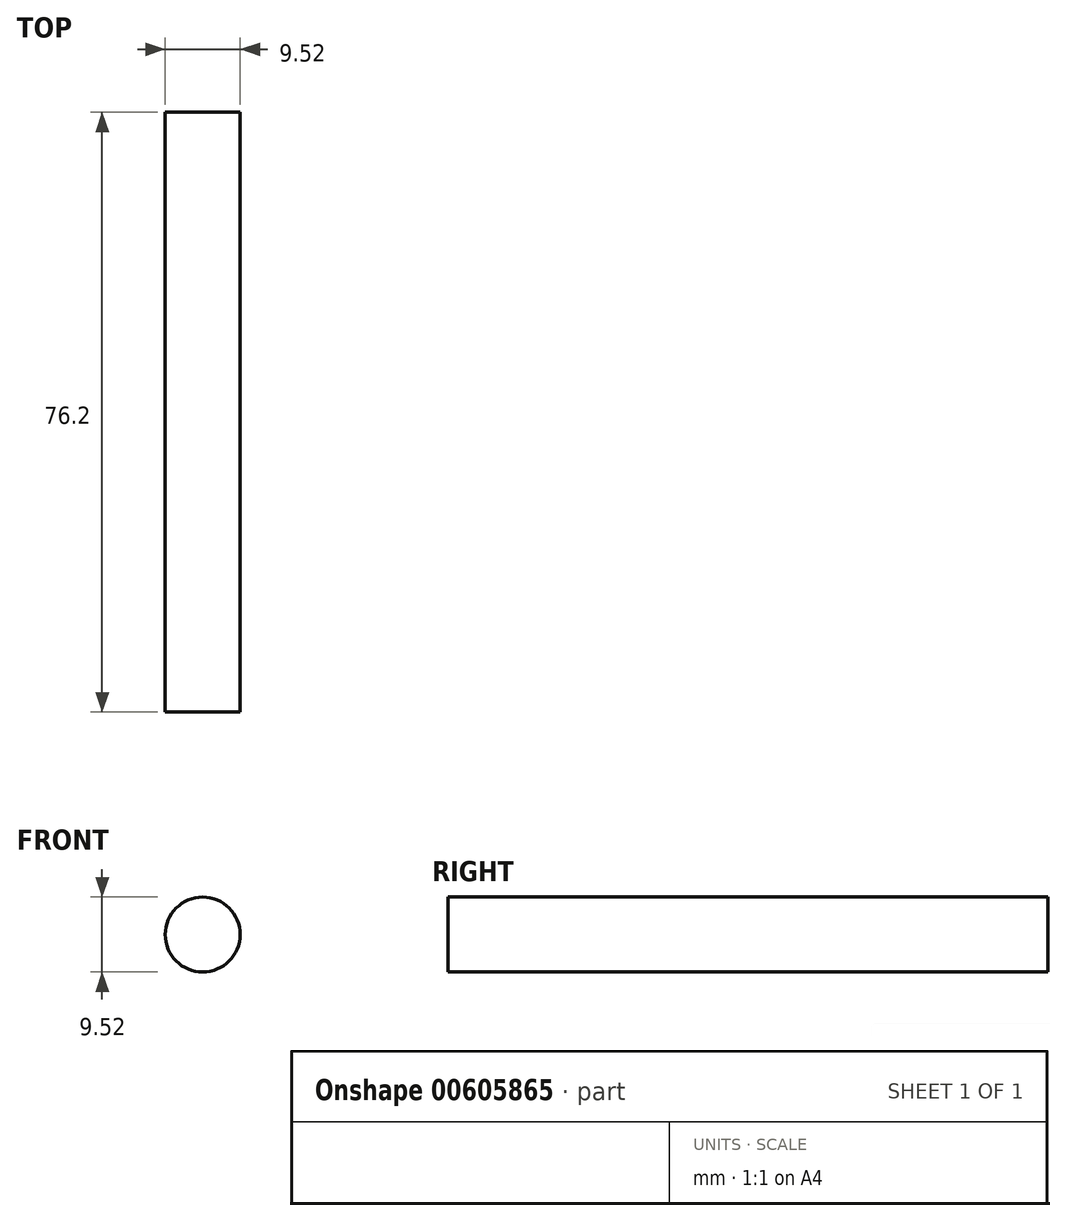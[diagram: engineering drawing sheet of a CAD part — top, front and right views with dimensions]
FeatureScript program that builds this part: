
annotation { "Feature Type Name" : "Feature", "Feature Type Description" : "" }
export const myFeature = defineFeature(function(context is Context, id is Id, definition is map)
    precondition{}
    {
        {
            var Q0;
            Q0=qCreatedBy(makeId("Front.planeOp"),FACE);
            var sketch = newSketch(context, id + "F0", { "sketchPlane" : qUnion([Q0])});
            skCircle(sketch, "E0", {"center": v(0, 0) * mm, "radius": 4.76 * mm});
            skSolve(sketch);
        }
        {
            var Q0;
            Q0=makeQuery(id+"F0.imprint","IMPRINT",FACE,{"disambiguationData":[TD([[makeQuery(id+"F0.imprint","IMPRINT",EDGE,{"derivedFrom":sQuery(id+"F0.wireOp",EDGE,"E0")}),1.0]])]});
            extrude(context, id + "F1", {"entities" : qUnion([Q0]), "oppositeDirection" : true, "depth" : 76.2 * mm, "offsetDistance" : 25.4 * mm});
        }
    });
